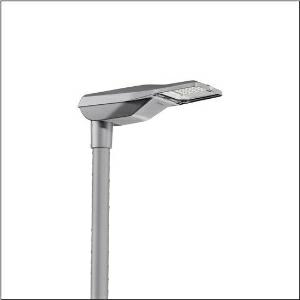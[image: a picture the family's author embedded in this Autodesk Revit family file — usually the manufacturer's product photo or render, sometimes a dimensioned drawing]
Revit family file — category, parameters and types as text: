
# Revit family: streetlight_sl_21_iq_micro___stw1_0a_5xe1e31g08db_041b
name_source: partatom
category: Lighting Fixtures
units: mm (PartAtom-declared; Revit-internal decimal feet)

## family parameters
Cut with Voids When Loaded = No
Host = Face
Light Source = No
Part Type = Normal
Room Calculation Point = No
Round Connector Dimension = Use Diameter
Shared = No

## types (1)
- --- (1 x LED, 4810 lm, 36.4 W, 3000K)
    Apparent Load = 36 VA
    CIE Flux Codes = 38 75 98 100 100
    Color Rendering = 70
    Color Temperature = 3000K
    Default Elevation = 1800 mm
    Description = Streetlight SL 21 iQ micro, mast luminaire, primary light control with lens, of PMMA, primary optical cover: cover, of toughened safety glass, transparent, light distribution: STW1.0a, light emission: direct distribution, primary light characteristic: asymmetric, installation type: post-top, side-entry, LED, High Power LED, rated luminous flux: 4.810lm, luminous efficacy: 132lm/W, light colour: 730, colour temperature: 3000K, control gear: iQ Street-Remote, control: Street-Remote, Auto-Match, Temp-Guard, Lumen-Switch, Night-Set, Smart-Wire, Light-Fading, Desk-Remote (wireless, voltage-free reading and setting of iQ features in the workshop via application-optimized NFC function/RFID function), optimised constant luminous flux control (CLO 2.0), pre-setting: linear dimming characteristic, mains connection: 220..240V, AC, 50/60Hz, start of lifetime: 36W, end of service life: 38W, reduction: 16W, luminaire housing, of diecast aluminium, powder-coated, SITECO metallic grey (DB 702S), corrosivity category C5 high according to DIN EN ISO 12944, please order mast flange separately, inclination adjustable: 0°, 5°, 10°, 15°, sealing non-destructively replaceable, multi-level sealing system, length: 528mm, width: 235mm, height: 110mm, mast flange for spigot size: 42mm (side-entry): 5XC10008XM4, 60/48mm (side-entry/post-top): 5XC10108XM2, 76/60mm (side-entry/post-top): 5XC10108XM1, protection rating (complete): IP66, insulation class (complete): insulation class II (safety insulation), certification: CE, ENEC, ENEC+, VDE, impact resistance: IK10, permissible operating ambient temperature for outdoor applications: -40..+50°C, standard-compliant lighting for roads and squares, packaging unit: 1 piece

Light Distribution: STW1.0a
    Height = 110 mm
    Lamp = 1 x LED
    Lamp Light Flux = 4810 lm
    Lamp Power = 36.4 W
    Lamp count = 1
    Length = 528 mm
    Luminous efficacy = 132 lm/W
    Manufacturer = Siteco
    ModVariant = No
    Model = 5XE1E31G08DB
    Number of Poles = 1
    OnlyDefault = Yes
    Power Factor = 1
    Product Name = Streetlight SL 21 iQ micro | STW1.0a
    Product group = mast luminaire | pylon top
    ProductGroupID = 6100
    Protection Class = Protection class II
    Protection Degree = IP 66
    RLX_Detail_Level = 1
    RLX_Emergency_Light_Flux = 0 lm
    RLX_Emergency_Type = 0
    RLX_Emergency_Type_DB = No
    RlxData = <blob elided: 99261 chars, md5=70949b0f>
    Socket = socket
    Standby Power = 0 W
    System Light Flux = 4810 lm
    System Power = 36 W
    Type Comments = factory setting: luminous flux: 100 % | dim-lin: 254 | 715 mA
    Type Image = l_1006881.jpg
    URL = http://relux.com
    VarID = @adj_154953
    Voltage = 0 V
    Weight = 0.00 kg
    Width = 235 mm

## geometry (parser evidence)
native form markers: Blend x4, Sweep x10
no freeform markers — native parametric forms only
